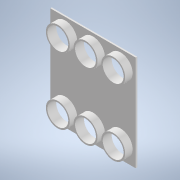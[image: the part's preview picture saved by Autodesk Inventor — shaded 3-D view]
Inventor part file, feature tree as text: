
AUTODESK INVENTOR PART (.ipt)
format: ipt  version: 2022 (Build 260153000, 153)  size: 161,792 bytes
history: native  units: mm
features: other x8, reference x6, extrude x2, sketch x2, projected_geometry x1
ambient origin geometry x8: Origin, YZ Plane, XZ Plane, XY Plane, X Axis, Y Axis, Z Axis, Center Point
bodies: Solid1 (feature_tree)
feature tree (19):
  extrude  "Extrusion1"  Depth=20.0mm
  extrude  "Extrusion2"  Depth=10.0mm
  sketch  "Sketch1"  dims[d0=20.0mm d1=20.0mm]
  reference  "Reference1"
  reference  "Reference2"
  reference  "Reference3"
  reference  "Reference4"
  reference  "Reference5"
  reference  "Reference6"
  sketch  "Sketch2"  dims[d2=20.0mm d3=20.0mm d4=0.3mm d5=0.3mm d6=0.3mm d7=0.3mm d8=0.3mm d9=0.3mm d10=2.0mm d11=0.0mm d12=2.0mm d13=2.0mm d14=2.0mm d15=2.0mm d16=2.0mm d17=2.0mm d18=10.0mm d19=0.0mm]
  projected_geometry  "Projected Loop1"
  other  "<userpath>\OneDrive - Imperial College London\ROBOICP\Final Assembly\Final Assembly.iam"
  other  "Final Assembly.iam"
  other  "vial:2"
  other  "vial:4"
  other  "vial:6"
  other  "vial:1"
  other  "vial:3"
  other  "vial:5"
